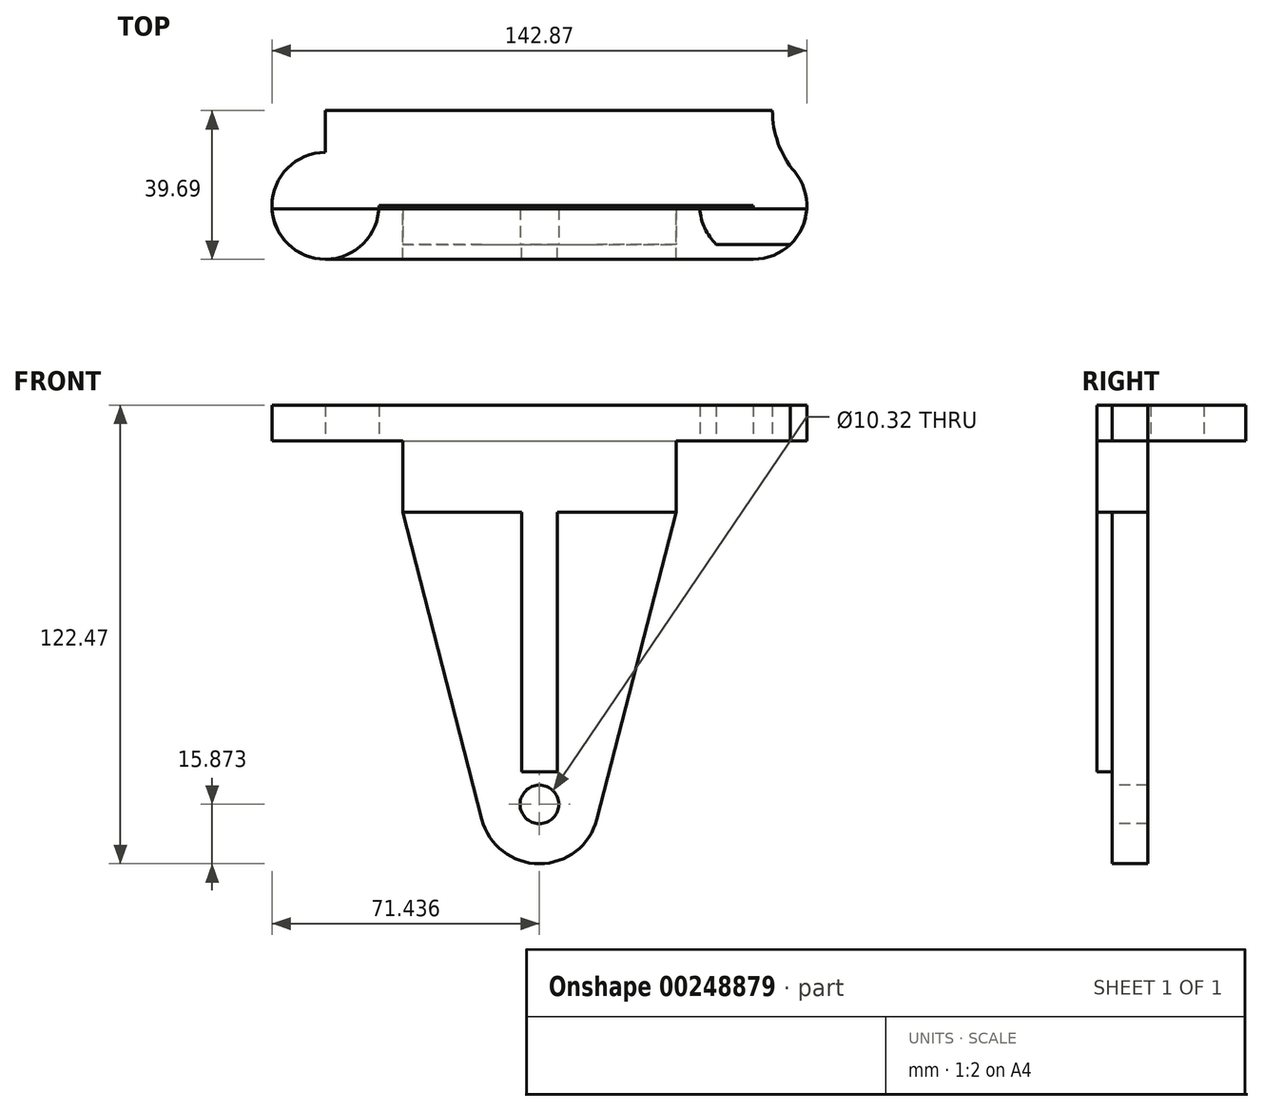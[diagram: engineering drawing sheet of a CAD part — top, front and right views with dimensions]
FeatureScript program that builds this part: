
annotation { "Feature Type Name" : "Feature", "Feature Type Description" : "" }
export const myFeature = defineFeature(function(context is Context, id is Id, definition is map)
    precondition{}
    {
        {
            var Q0;
            Q0=qCreatedBy(makeId("Front.planeOp"),FACE);
            var sketch = newSketch(context, id + "F0", { "sketchPlane" : qUnion([Q0])});
            skLineSegment(sketch, "E0", {"start": v(-41.2, 23.17) * mm, "end": v(-9.46, 23.17) * mm});
            skLineSegment(sketch, "E1", {"start": v(31.82, 23.17) * mm, "end": v(10.53, -59.38) * mm});
            skLineSegment(sketch, "E2", {"start": v(-19.92, -59.38) * mm, "end": v(-41.2, 23.17) * mm});
            skPoint(sketch, "E3", {"position": v(-4.7, -54.86) * mm});
            skArc(sketch, "E4", {"start": v(-20.07, -58.82) * mm, "mid": v(-4.7, -70.73) * mm, "end": v(10.68, -58.82) * mm});
            skLineSegment(sketch, "E5", {"start": v(-41.2, 23.17) * mm, "end": v(-41.2, 42.22) * mm});
            skLineSegment(sketch, "E6", {"start": v(31.82, 42.22) * mm, "end": v(31.82, 23.17) * mm});
            skPoint(sketch, "E7", {"position": v(-4.7, 42.22) * mm});
            skLineSegment(sketch, "E8", {"start": v(31.82, 42.22) * mm, "end": v(52.46, 42.22) * mm});
            skLineSegment(sketch, "E9", {"start": v(-41.2, 42.22) * mm, "end": v(-61.84, 42.22) * mm});
            skLineSegment(sketch, "E10", {"start": v(-61.84, 42.22) * mm, "end": v(-76.13, 42.22) * mm});
            skLineSegment(sketch, "E11", {"start": v(-76.13, 42.22) * mm, "end": v(-76.13, 51.74) * mm});
            skLineSegment(sketch, "E12", {"start": v(-76.13, 51.74) * mm, "end": v(66.74, 51.74) * mm});
            skLineSegment(sketch, "E13", {"start": v(66.74, 51.74) * mm, "end": v(66.74, 42.22) * mm});
            skLineSegment(sketch, "E14", {"start": v(66.74, 42.22) * mm, "end": v(52.46, 42.22) * mm});
            skPoint(sketch, "E15", {"position": v(-4.7, 23.17) * mm});
            skLineSegment(sketch, "E16", {"start": v(-9.46, 23.17) * mm, "end": v(-9.46, -46.13) * mm});
            skLineSegment(sketch, "E17", {"start": v(0.07, 23.17) * mm, "end": v(0.07, -46.13) * mm});
            skLineSegment(sketch, "E18", {"start": v(-9.46, -46.13) * mm, "end": v(0.07, -46.13) * mm});
            skCircle(sketch, "E19", {"center": v(-4.7, -54.86) * mm, "radius": 5.16 * mm});
            skLineSegment(sketch, "E20.trimOffspring", {"start": v(0.07, 23.17) * mm, "end": v(31.82, 23.17) * mm});
            skSolve(sketch);
        }
        {
            var Q0;
            Q0=makeQuery(id+"F0.imprint","IMPRINT",FACE,{"disambiguationData":[TD([[makeQuery(id+"F0.imprint","IMPRINT",EDGE,{"derivedFrom":sQuery(id+"F0.wireOp",EDGE,"E0")}),1.0]])]});
            extrude(context, id + "F1", {"entities" : qUnion([Q0]), "depth" : 3.97 * mm});
        }
        {
            var Q0;
            {var subQ2=sQuery(id+"F0.wireOp",EDGE,"E0");Q0=makeQuery(id+"F0.imprint","IMPRINT",FACE,{"disambiguationData":[TD([[makeQuery(id+"F0.imprint","IMPRINT",EDGE,{"derivedFrom":subQ2}),-1.0]])]});}
            var Q1;
            Q1=makeQuery(id+"F0.imprint","IMPRINT",FACE,{"disambiguationData":[TD([[makeQuery(id+"F0.imprint","IMPRINT",EDGE,{"derivedFrom":sQuery(id+"F0.wireOp",EDGE,"E0")}),1.0]])]});
            extrude(context, id + "F2", {"entities" : qUnion([Q0, Q1]), "oppositeDirection" : true, "depth" : 9.52 * mm});
        }
        {
            var Q0;
            Q0=makeQuery(id+"F2.opExtrude","SWEPT_FACE",FACE,{"disambiguationData":[OSD([sQuery(id+"F0.wireOp",EDGE,"E8"),sQuery(id+"F0.wireOp",EDGE,"E14")])]});
            var sketch = newSketch(context, id + "F3", { "sketchPlane" : qUnion([Q0])});
            skArc(sketch, "E21", {"start": v(63.43, -19.46) * mm, "mid": v(59.07, -27.07) * mm, "end": v(57.55, -35.72) * mm});
            skCircle(sketch, "E22", {"center": v(52.46, -10.32) * mm, "radius": 14.29 * mm});
            skLineSegment(sketch, "E23", {"start": v(52.46, -10.32) * mm, "end": v(52.46, -35.72) * mm});
            skLineSegment(sketch, "E24", {"start": v(52.46, -10.32) * mm, "end": v(-4.7, -10.32) * mm});
            skLineSegment(sketch, "E25", {"start": v(-4.7, -10.32) * mm, "end": v(-4.7, -35.72) * mm});
            skLineSegment(sketch, "E26.MirrorCS", {"start": v(-61.84, -10.32) * mm, "end": v(-4.7, -10.32) * mm});
            skLineSegment(sketch, "E27.MirrorCS", {"start": v(-61.84, -10.32) * mm, "end": v(-61.84, -35.72) * mm});
            skCircle(sketch, "E28.MirrorC", {"center": v(-61.84, -10.32) * mm, "radius": 14.29 * mm});
            skArc(sketch, "E29.MirrorCS", {"start": v(-72.82, -19.46) * mm, "mid": v(-68.45, -27.07) * mm, "end": v(-66.94, -35.72) * mm});
            skLineSegment(sketch, "E30", {"start": v(-66.94, -35.72) * mm, "end": v(57.55, -35.72) * mm});
            skPoint(sketch, "E31.orphan", {"position": v(-72.82, -51.97) * mm});
            skPoint(sketch, "E32.MirrorC.center.orphan", {"position": v(-61.84, -61.12) * mm});
            skPoint(sketch, "E33.center.orphan", {"position": v(52.46, -61.12) * mm});
            skPoint(sketch, "E34.orphan", {"position": v(63.43, -51.97) * mm});
            skLineSegment(sketch, "E35", {"start": v(-61.84, -10.32) * mm, "end": v(-61.84, -9.54) * mm});
            skLineSegment(sketch, "E36", {"start": v(52.46, -10.32) * mm, "end": v(52.46, -9.53) * mm});
            skSolve(sketch);
        }
        {
            var Q0;
            {var subQ0=sQuery(id+"F3.wireOp",EDGE,"E27.MirrorCS");var subQ1=sQuery(id+"F3.wireOp",EDGE,"E26.MirrorCS");var subQ2=makeQuery(id+"F3.imprint","INTERSECT",VERTEX,{"derivedFrom":[subQ1,subQ0]});Q0=makeQuery(id+"F3.imprint","IMPRINT",FACE,{"disambiguationData":[TD([[makeQuery(id+"F3.imprint","IMPRINT",EDGE,{"disambiguationData":[TD([[subQ2,-1.0]])],"derivedFrom":subQ1}),-1.0]])]});}
            var Q1;
            {var subQ5=sQuery(id+"F3.wireOp",EDGE,"E29.MirrorCS");Q1=makeQuery(id+"F3.imprint","IMPRINT",FACE,{"disambiguationData":[TD([[makeQuery(id+"F3.imprint","IMPRINT",EDGE,{"derivedFrom":subQ5}),1.0]])]});}
            var Q2;
            {var subQ7=sQuery(id+"F3.wireOp",EDGE,"E25");Q2=makeQuery(id+"F3.imprint","IMPRINT",FACE,{"disambiguationData":[TD([[makeQuery(id+"F3.imprint","IMPRINT",EDGE,{"derivedFrom":subQ7}),-1.0]])]});}
            var Q3;
            {var subQ0=sQuery(id+"F3.wireOp",EDGE,"E25");Q3=makeQuery(id+"F3.imprint","IMPRINT",FACE,{"disambiguationData":[TD([[makeQuery(id+"F3.imprint","IMPRINT",EDGE,{"derivedFrom":subQ0}),1.0]])]});}
            var Q4;
            {var subQ0=sQuery(id+"F3.wireOp",EDGE,"E21");Q4=makeQuery(id+"F3.imprint","IMPRINT",FACE,{"disambiguationData":[TD([[makeQuery(id+"F3.imprint","IMPRINT",EDGE,{"derivedFrom":subQ0}),-1.0]])]});}
            var Q5;
            {var subQ0=sQuery(id+"F3.wireOp",EDGE,"E27.MirrorCS");var subQ1=sQuery(id+"F3.wireOp",EDGE,"E26.MirrorCS");var subQ2=makeQuery(id+"F3.imprint","INTERSECT",VERTEX,{"derivedFrom":[subQ1,subQ0]});Q5=makeQuery(id+"F3.imprint","IMPRINT",FACE,{"disambiguationData":[TD([[makeQuery(id+"F3.imprint","IMPRINT",EDGE,{"disambiguationData":[TD([[subQ2,-1.0]])],"derivedFrom":subQ1}),1.0]])]});}
            var Q6;
            {var subQ3=sQuery(id+"F3.wireOp",EDGE,"E22");var subQ5=makeQuery(id+"F3.imprint","INTERSECT",VERTEX,{"derivedFrom":[sQuery(id+"F3.wireOp",EDGE,"E21"),subQ3]});Q6=makeQuery(id+"F3.imprint","IMPRINT",FACE,{"disambiguationData":[TD([[makeQuery(id+"F3.imprint","IMPRINT",EDGE,{"disambiguationData":[TD([[subQ5,1.0]])],"derivedFrom":subQ3}),1.0]])]});}
            var Q7;
            {var subQ0=sQuery(id+"F3.wireOp",EDGE,"E22");var subQ1=sQuery(id+"F0.wireOp",EDGE,"E14");var subQ2=sQuery(id+"F0.wireOp",EDGE,"E8");var subQ3=makeQuery(id+"F2.opExtrude","CAP_EDGE",EDGE,{"disambiguationData":[OSD([subQ2,subQ1])],"isStart":true});var subQ4=makeQuery(id+"F3.imprint","INTERSECT",VERTEX,{"disambiguationData":[OD(0.0)],"derivedFrom":[subQ3,subQ0]});Q7=makeQuery(id+"F3.imprint","IMPRINT",FACE,{"disambiguationData":[TD([[makeQuery(id+"F3.imprint","IMPRINT",EDGE,{"disambiguationData":[TD([[subQ4,1.0]])],"derivedFrom":subQ0}),1.0]])]});}
            var Q8;
            {var subQ0=sQuery(id+"F3.wireOp",EDGE,"E24");var subQ1=sQuery(id+"F3.wireOp",EDGE,"E22");var subQ2=makeQuery(id+"F3.imprint","INTERSECT",VERTEX,{"derivedFrom":[subQ1,subQ0]});Q8=makeQuery(id+"F3.imprint","IMPRINT",FACE,{"disambiguationData":[TD([[makeQuery(id+"F3.imprint","IMPRINT",EDGE,{"disambiguationData":[TD([[subQ2,-1.0]])],"derivedFrom":subQ1}),1.0]])]});}
            extrude(context, id + "F4", {"entities" : qUnion([Q0, Q1, Q2, Q3, Q4, Q5, Q6, Q7, Q8]), "oppositeDirection" : true, "depth" : 9.52 * mm});
        }
        {
            var Q0;
            Q0=makeQuery(id+"F1.opExtrude","SWEPT_BODY",BODY,{"disambiguationData":[OSD([sQuery(id+"F0.wireOp",EDGE,"E0"),sQuery(id+"F0.wireOp",EDGE,"E5"),sQuery(id+"F0.wireOp",EDGE,"E6"),sQuery(id+"F0.wireOp",EDGE,"E8"),sQuery(id+"F0.wireOp",EDGE,"E9"),sQuery(id+"F0.wireOp",EDGE,"E10"),sQuery(id+"F0.wireOp",EDGE,"E11"),sQuery(id+"F0.wireOp",EDGE,"E12"),sQuery(id+"F0.wireOp",EDGE,"E13"),sQuery(id+"F0.wireOp",EDGE,"E14"),sQuery(id+"F0.wireOp",EDGE,"E16"),sQuery(id+"F0.wireOp",EDGE,"E17"),sQuery(id+"F0.wireOp",EDGE,"E18"),sQuery(id+"F0.wireOp",EDGE,"E20.trimOffspring")])]});
            var Q1;
            Q1=makeQuery(id+"F2.opExtrude","SWEPT_BODY",BODY,{"disambiguationData":[OSD([sQuery(id+"F0.wireOp",EDGE,"E1"),sQuery(id+"F0.wireOp",EDGE,"E2"),sQuery(id+"F0.wireOp",EDGE,"E4"),sQuery(id+"F0.wireOp",EDGE,"E5"),sQuery(id+"F0.wireOp",EDGE,"E6"),sQuery(id+"F0.wireOp",EDGE,"E8"),sQuery(id+"F0.wireOp",EDGE,"E9"),sQuery(id+"F0.wireOp",EDGE,"E10"),sQuery(id+"F0.wireOp",EDGE,"E11"),sQuery(id+"F0.wireOp",EDGE,"E12"),sQuery(id+"F0.wireOp",EDGE,"E13"),sQuery(id+"F0.wireOp",EDGE,"E14"),sQuery(id+"F0.wireOp",EDGE,"E19")])]});
            booleanBodies(context, id + "F5", {"operationType" : BooleanOperationType.UNION, "tools" : qUnion([Q0, Q1])});
        }
        {
            var Q0;
            {var subQ0=sQuery(id+"F0.wireOp",EDGE,"E14");var subQ1=sQuery(id+"F0.wireOp",EDGE,"E8");Q0=makeQuery(id+"F5.opBoolean","MERGE",FACE,{"derivedFrom":[makeQuery(id+"F1.opExtrude","SWEPT_FACE",FACE,{"disambiguationData":[OSD([subQ1,subQ0])]}),makeQuery(id+"F2.opExtrude","SWEPT_FACE",FACE,{"disambiguationData":[OSD([subQ1,subQ0])]})]});}
            var sketch = newSketch(context, id + "F6", { "sketchPlane" : qUnion([Q0])});
            skLineSegment(sketch, "E37", {"start": v(52.46, 3.97) * mm, "end": v(58.85, 3.97) * mm});
            skLineSegment(sketch, "E38", {"start": v(66.74, -2.78) * mm, "end": v(66.74, -10.32) * mm});
            skPoint(sketch, "E39.visualSharp", {"position": v(66.74, 3.97) * mm});
            skArc(sketch, "E39.filletArc", {"start": v(66.74, -10.32) * mm, "mid": v(62.56, -0.22) * mm, "end": v(52.46, 3.97) * mm});
            skSolve(sketch);
        }
        {
            var Q0;
            {var subQ0=sQuery(id+"F0.wireOp",EDGE,"E10");var subQ1=sQuery(id+"F0.wireOp",EDGE,"E9");Q0=makeQuery(id+"F5.opBoolean","MERGE",FACE,{"derivedFrom":[makeQuery(id+"F1.opExtrude","SWEPT_FACE",FACE,{"disambiguationData":[OSD([subQ1,subQ0])]}),makeQuery(id+"F2.opExtrude","SWEPT_FACE",FACE,{"disambiguationData":[OSD([subQ1,subQ0])]})]});}
            var sketch = newSketch(context, id + "F7", { "sketchPlane" : qUnion([Q0])});
            skLineSegment(sketch, "E40", {"start": v(-76.13, -10.32) * mm, "end": v(-76.13, -2.78) * mm});
            skLineSegment(sketch, "E41", {"start": v(-69.37, 3.97) * mm, "end": v(-61.84, 3.97) * mm});
            skPoint(sketch, "E42.visualSharp", {"position": v(-76.13, 3.97) * mm});
            skArc(sketch, "E42.filletArc", {"start": v(-61.84, 3.97) * mm, "mid": v(-71.95, -0.22) * mm, "end": v(-76.13, -10.32) * mm});
            skSolve(sketch);
        }
        {
            var Q0;
            {var subQ5=sQuery(id+"F7.wireOp",EDGE,"E41");Q0=makeQuery(id+"F7.imprint","IMPRINT",FACE,{"disambiguationData":[TD([[makeQuery(id+"F7.imprint","IMPRINT",EDGE,{"derivedFrom":subQ5}),1.0]])]});}
            var Q1;
            {var subQ9=sQuery(id+"F6.wireOp",EDGE,"E37");Q1=makeQuery(id+"F6.imprint","IMPRINT",FACE,{"disambiguationData":[TD([[makeQuery(id+"F6.imprint","IMPRINT",EDGE,{"derivedFrom":subQ9}),-1.0]])]});}
            extrude(context, id + "F8", {"entities" : qUnion([Q0, Q1]), "operationType" : NewBodyOperationType.REMOVE, "endBound" : BoundingType.THROUGH_ALL, "oppositeDirection" : true, "depth" : 25.4 * mm});
        }
    });
